# Revit family: SFD-RWL-HAS-Soldier_Pile
name_source: partatom
category: Structural Foundations
revit_build: Autodesk Revit 2016 (Build: 20150220_1215(x64)
units: mm (PartAtom-declared; Revit-internal decimal feet)

## family parameters
Always vertical = Yes
Cap = No
Cut with Voids When Loaded = No
Material for Model Behavior = Steel
Shared = Yes
Work Plane-Based = Yes

## types (4) — shared parameters
Default Elevation = 1219 mm

## per-type parameters (varying)
| type | B | D | Description | Manufacturer | Type Comments | tf | tw |
| 305x305x186 kg/m | 320 mm | 327 mm | 305x305x180 kg/m H-PILE | Dragon Steel | S450J0 | 25 mm  [stored 0.082021 ft] | 25 mm  [stored 0.082021 ft] |
| 305x305x223 kg/m | 325 mm | 338 mm | 305x305x223 kg/m H-PILE |  | BS4:Part 1 | 31 mm | 31 mm |
| 305x305x180 kg/m | 320 mm | 327 mm | 305x305x180 kg/m H-PILE | Dragon Steel | S450J0 | 25 mm  [stored 0.082021 ft] | 25 mm  [stored 0.082021 ft] |
| 356x368x174 kg/m | 378 mm | 362 mm | 356x368x174 kg/m H-PILE |  | BS4:Part 1 | 20 mm | 20 mm |

note: [stored X ft] marks values corroborated as IEEE doubles in the binary element streams (Revit-internal decimal feet)

## geometry (parser evidence)
native form markers: Blend x8
no freeform markers — native parametric forms only
